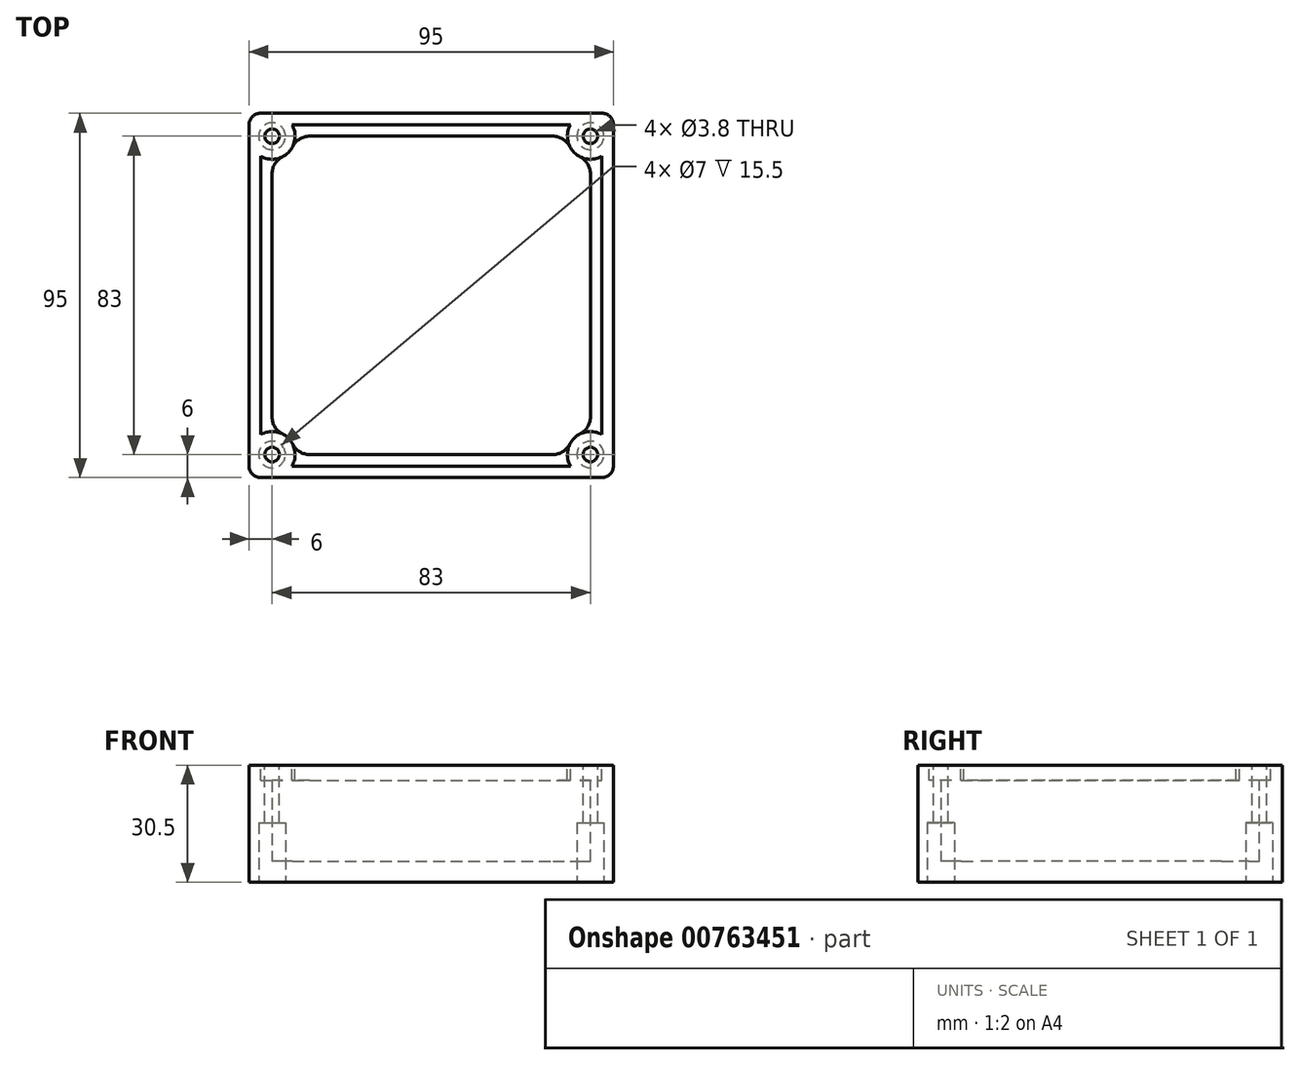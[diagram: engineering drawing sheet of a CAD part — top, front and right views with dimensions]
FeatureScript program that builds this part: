
annotation { "Feature Type Name" : "Feature", "Feature Type Description" : "" }
export const myFeature = defineFeature(function(context is Context, id is Id, definition is map)
    precondition{}
    {
        {
            var Q0;
            Q0=qCreatedBy(makeId("Top.planeOp"),FACE);
            var sketch = newSketch(context, id + "F0", { "sketchPlane" : qUnion([Q0])});
            skLineSegment(sketch, "E0.bottom", {"start": v(-47.5, 47.5) * mm, "end": v(47.5, 47.5) * mm});
            skLineSegment(sketch, "E0.top", {"start": v(-47.5, -47.5) * mm, "end": v(47.5, -47.5) * mm});
            skLineSegment(sketch, "E0.left", {"start": v(-47.5, 47.5) * mm, "end": v(-47.5, -47.5) * mm});
            skLineSegment(sketch, "E0.right", {"start": v(47.5, 47.5) * mm, "end": v(47.5, -47.5) * mm});
            skSolve(sketch);
        }
        {
            var Q0;
            Q0 = qSketchRegion(id + "F0", true);
            extrude(context, id + "F1", {"entities" : qUnion([Q0]), "depth" : 30.5 * mm, "offsetDistance" : 25 * mm});
        }
        {
            var Q0;
            Q0=makeQuery(id+"F1.opExtrude","CAP_FACE",FACE,{"disambiguationData":[OSD([sQuery(id+"F0.wireOp",EDGE,"E0.bottom"),sQuery(id+"F0.wireOp",EDGE,"E0.top"),sQuery(id+"F0.wireOp",EDGE,"E0.left"),sQuery(id+"F0.wireOp",EDGE,"E0.right")])],"isStart":false});
            var sketch = newSketch(context, id + "F2", { "sketchPlane" : qUnion([Q0])});
            skLineSegment(sketch, "E1.bottom", {"start": v(-47.5, 47.5) * mm, "end": v(-41.5, 47.5) * mm});
            skLineSegment(sketch, "E1.top", {"start": v(-47.5, 41.5) * mm, "end": v(-41.5, 41.5) * mm});
            skLineSegment(sketch, "E1.left", {"start": v(-47.5, 47.5) * mm, "end": v(-47.5, 41.5) * mm});
            skLineSegment(sketch, "E1.right", {"start": v(-41.5, 47.5) * mm, "end": v(-41.5, 41.5) * mm});
            skLineSegment(sketch, "E2.bottom", {"start": v(-47.5, -47.5) * mm, "end": v(-41.5, -47.5) * mm});
            skLineSegment(sketch, "E2.top", {"start": v(-47.5, -41.5) * mm, "end": v(-41.5, -41.5) * mm});
            skLineSegment(sketch, "E2.left", {"start": v(-47.5, -47.5) * mm, "end": v(-47.5, -41.5) * mm});
            skLineSegment(sketch, "E2.right", {"start": v(-41.5, -47.5) * mm, "end": v(-41.5, -41.5) * mm});
            skLineSegment(sketch, "E3.bottom", {"start": v(47.5, -47.5) * mm, "end": v(41.5, -47.5) * mm});
            skLineSegment(sketch, "E3.top", {"start": v(47.5, -41.5) * mm, "end": v(41.5, -41.5) * mm});
            skLineSegment(sketch, "E3.left", {"start": v(47.5, -47.5) * mm, "end": v(47.5, -41.5) * mm});
            skLineSegment(sketch, "E3.right", {"start": v(41.5, -47.5) * mm, "end": v(41.5, -41.5) * mm});
            skLineSegment(sketch, "E4.bottom", {"start": v(47.5, 47.5) * mm, "end": v(41.5, 47.5) * mm});
            skLineSegment(sketch, "E4.top", {"start": v(47.5, 41.5) * mm, "end": v(41.5, 41.5) * mm});
            skLineSegment(sketch, "E4.left", {"start": v(47.5, 47.5) * mm, "end": v(47.5, 41.5) * mm});
            skLineSegment(sketch, "E4.right", {"start": v(41.5, 47.5) * mm, "end": v(41.5, 41.5) * mm});
            skCircle(sketch, "E5", {"center": v(-41.5, 41.5) * mm, "radius": 6 * mm});
            skCircle(sketch, "E6", {"center": v(41.5, 41.5) * mm, "radius": 6 * mm});
            skCircle(sketch, "E7", {"center": v(41.5, -41.5) * mm, "radius": 6 * mm});
            skCircle(sketch, "E8", {"center": v(-41.5, -41.5) * mm, "radius": 6 * mm});
            skLineSegment(sketch, "E9.bottom", {"start": v(-47.5, 47.5) * mm, "end": v(-44.5, 47.5) * mm});
            skLineSegment(sketch, "E9.top", {"start": v(-47.5, -47.5) * mm, "end": v(-44.5, -47.5) * mm});
            skLineSegment(sketch, "E9.left", {"start": v(-47.5, 47.5) * mm, "end": v(-47.5, -47.5) * mm});
            skLineSegment(sketch, "E9.right", {"start": v(-44.5, 47.5) * mm, "end": v(-44.5, -47.5) * mm});
            skLineSegment(sketch, "E10.bottom", {"start": v(-47.5, -44.5) * mm, "end": v(47.5, -44.5) * mm});
            skLineSegment(sketch, "E10.top", {"start": v(-47.5, -47.5) * mm, "end": v(47.5, -47.5) * mm});
            skLineSegment(sketch, "E10.left", {"start": v(-47.5, -44.5) * mm, "end": v(-47.5, -47.5) * mm});
            skLineSegment(sketch, "E10.right", {"start": v(47.5, -44.5) * mm, "end": v(47.5, -47.5) * mm});
            skLineSegment(sketch, "E11.bottom", {"start": v(44.5, -47.5) * mm, "end": v(47.5, -47.5) * mm});
            skLineSegment(sketch, "E11.top", {"start": v(44.5, 47.5) * mm, "end": v(47.5, 47.5) * mm});
            skLineSegment(sketch, "E11.left", {"start": v(44.5, -47.5) * mm, "end": v(44.5, 47.5) * mm});
            skLineSegment(sketch, "E11.right", {"start": v(47.5, -47.5) * mm, "end": v(47.5, 47.5) * mm});
            skLineSegment(sketch, "E12.bottom", {"start": v(47.5, 44.5) * mm, "end": v(-47.5, 44.5) * mm});
            skLineSegment(sketch, "E12.top", {"start": v(47.5, 47.5) * mm, "end": v(-47.5, 47.5) * mm});
            skLineSegment(sketch, "E12.left", {"start": v(47.5, 44.5) * mm, "end": v(47.5, 47.5) * mm});
            skLineSegment(sketch, "E12.right", {"start": v(-47.5, 44.5) * mm, "end": v(-47.5, 47.5) * mm});
            skSolve(sketch);
        }
        {
            var Q0;
            {var subQ9=sQuery(id+"F2.wireOp",EDGE,"E12.bottom");var subQ10=sQuery(id+"F2.wireOp",EDGE,"E5");var subQ11=makeQuery(id+"F2.imprint","INTERSECT",VERTEX,{"disambiguationData":[OD(0.0)],"derivedFrom":[subQ10,subQ9]});Q0=makeQuery(id+"F2.imprint","IMPRINT",FACE,{"disambiguationData":[TD([[makeQuery(id+"F2.imprint","IMPRINT",EDGE,{"disambiguationData":[TD([[subQ11,1.0]])],"derivedFrom":subQ10}),-1.0]])]});}
            extrude(context, id + "F3", {"entities" : qUnion([Q0]), "operationType" : NewBodyOperationType.REMOVE, "oppositeDirection" : true, "depth" : 25 * mm, "offsetDistance" : 25 * mm});
        }
        {
            var Q0;
            Q0=makeQuery(id+"F1.opExtrude","CAP_FACE",FACE,{"disambiguationData":[OSD([sQuery(id+"F0.wireOp",EDGE,"E0.bottom"),sQuery(id+"F0.wireOp",EDGE,"E0.top"),sQuery(id+"F0.wireOp",EDGE,"E0.left"),sQuery(id+"F0.wireOp",EDGE,"E0.right")])],"isStart":false});
            var sketch = newSketch(context, id + "F4", { "sketchPlane" : qUnion([Q0])});
            skCircle(sketch, "E13", {"center": v(-41.5, 41.5) * mm, "radius": 1.9 * mm});
            skCircle(sketch, "E14", {"center": v(41.5, 41.5) * mm, "radius": 1.9 * mm});
            skCircle(sketch, "E15", {"center": v(-41.5, -41.5) * mm, "radius": 1.9 * mm});
            skCircle(sketch, "E16", {"center": v(41.5, -41.5) * mm, "radius": 1.9 * mm});
            skSolve(sketch);
        }
        {
            var Q0;
            Q0 = qSketchRegion(id + "F4", true);
            extrude(context, id + "F5", {"entities" : qUnion([Q0]), "operationType" : NewBodyOperationType.REMOVE, "endBound" : BoundingType.THROUGH_ALL, "oppositeDirection" : true, "depth" : 25 * mm, "offsetDistance" : 25 * mm});
        }
        {
            var Q0;
            Q0=makeQuery(id+"F1.opExtrude","SWEPT_EDGE",EDGE,{"disambiguationData":[OSD([sQuery(id+"F0.wireOp",EDGE,"E0.bottom"),sQuery(id+"F0.wireOp",EDGE,"E0.left")])]});
            var Q1;
            Q1=makeQuery(id+"F1.opExtrude","SWEPT_EDGE",EDGE,{"disambiguationData":[OSD([sQuery(id+"F0.wireOp",EDGE,"E0.bottom"),sQuery(id+"F0.wireOp",EDGE,"E0.right")])]});
            var Q2;
            Q2=makeQuery(id+"F1.opExtrude","SWEPT_EDGE",EDGE,{"disambiguationData":[OSD([sQuery(id+"F0.wireOp",EDGE,"E0.top"),sQuery(id+"F0.wireOp",EDGE,"E0.left")])]});
            var Q3;
            Q3=makeQuery(id+"F1.opExtrude","SWEPT_EDGE",EDGE,{"disambiguationData":[OSD([sQuery(id+"F0.wireOp",EDGE,"E0.top"),sQuery(id+"F0.wireOp",EDGE,"E0.right")])]});
            fillet(context, id + "F6", {"entities" : qUnion([Q0, Q1, Q2, Q3]), "radius" : 3 * mm, "tangentPropagation" : true, "allowEdgeOverflow" : false});
        }
        {
            var Q0;
            Q0=makeQuery(id+"F3.boolean.opBoolean","COPY",FACE,{"derivedFrom":makeQuery(id+"F3.opExtrude","CAP_FACE",FACE,{"disambiguationData":[OSD([sQuery(id+"F2.wireOp",EDGE,"E5"),sQuery(id+"F2.wireOp",EDGE,"E6"),sQuery(id+"F2.wireOp",EDGE,"E7"),sQuery(id+"F2.wireOp",EDGE,"E8"),sQuery(id+"F2.wireOp",EDGE,"E9.right"),sQuery(id+"F2.wireOp",EDGE,"E10.bottom"),sQuery(id+"F2.wireOp",EDGE,"E11.left"),sQuery(id+"F2.wireOp",EDGE,"E12.bottom")])],"isStart":false})});
            var sketch = newSketch(context, id + "F7", { "sketchPlane" : qUnion([Q0])});
            skLineSegment(sketch, "E17.bottom", {"start": v(-36.3, 44.5) * mm, "end": v(36.3, 44.5) * mm});
            skLineSegment(sketch, "E17.top", {"start": v(-36.3, 41.5) * mm, "end": v(36.3, 41.5) * mm});
            skLineSegment(sketch, "E17.left", {"start": v(-36.3, 44.5) * mm, "end": v(-36.3, 41.5) * mm});
            skLineSegment(sketch, "E17.right", {"start": v(36.3, 44.5) * mm, "end": v(36.3, 41.5) * mm});
            skLineSegment(sketch, "E18.bottom", {"start": v(-44.5, 36.3) * mm, "end": v(-41.5, 36.3) * mm});
            skLineSegment(sketch, "E18.top", {"start": v(-44.5, -36.3) * mm, "end": v(-41.5, -36.3) * mm});
            skLineSegment(sketch, "E18.left", {"start": v(-44.5, 36.3) * mm, "end": v(-44.5, -36.3) * mm});
            skLineSegment(sketch, "E18.right", {"start": v(-41.5, 36.3) * mm, "end": v(-41.5, -36.3) * mm});
            skLineSegment(sketch, "E19.bottom", {"start": v(-36.3, -44.5) * mm, "end": v(36.3, -44.5) * mm});
            skLineSegment(sketch, "E19.top", {"start": v(-36.3, -41.5) * mm, "end": v(36.3, -41.5) * mm});
            skLineSegment(sketch, "E19.left", {"start": v(-36.3, -44.5) * mm, "end": v(-36.3, -41.5) * mm});
            skLineSegment(sketch, "E19.right", {"start": v(36.3, -44.5) * mm, "end": v(36.3, -41.5) * mm});
            skLineSegment(sketch, "E20.bottom", {"start": v(44.5, 36.3) * mm, "end": v(41.5, 36.3) * mm});
            skLineSegment(sketch, "E20.top", {"start": v(44.5, -36.3) * mm, "end": v(41.5, -36.3) * mm});
            skLineSegment(sketch, "E20.left", {"start": v(44.5, 36.3) * mm, "end": v(44.5, -36.3) * mm});
            skLineSegment(sketch, "E20.right", {"start": v(41.5, 36.3) * mm, "end": v(41.5, -36.3) * mm});
            skSolve(sketch);
        }
        {
            var Q0;
            Q0 = qSketchRegion(id + "F7", true);
            extrude(context, id + "F8", {"entities" : qUnion([Q0]), "operationType" : NewBodyOperationType.ADD, "depth" : 21 * mm, "offsetDistance" : 25 * mm});
        }
        {
            var Q0;
            Q0=makeQuery(id+"F8.boolean.opBoolean","INTERSECT",EDGE,{"derivedFrom":[makeQuery(id+"F3.boolean.opBoolean","COPY",FACE,{"derivedFrom":makeQuery(id+"F3.opExtrude","SWEPT_FACE",FACE,{"disambiguationData":[OSD([sQuery(id+"F2.wireOp",EDGE,"E5")])]})}),makeQuery(id+"F8.opExtrude","SWEPT_FACE",FACE,{"disambiguationData":[OSD([sQuery(id+"F7.wireOp",EDGE,"E17.top")])]})]});
            var Q1;
            Q1=makeQuery(id+"F8.boolean.opBoolean","INTERSECT",EDGE,{"derivedFrom":[makeQuery(id+"F3.boolean.opBoolean","COPY",FACE,{"derivedFrom":makeQuery(id+"F3.opExtrude","SWEPT_FACE",FACE,{"disambiguationData":[OSD([sQuery(id+"F2.wireOp",EDGE,"E5")])]})}),makeQuery(id+"F8.opExtrude","SWEPT_FACE",FACE,{"disambiguationData":[OSD([sQuery(id+"F7.wireOp",EDGE,"E18.right")])]})]});
            var Q2;
            Q2=makeQuery(id+"F8.boolean.opBoolean","INTERSECT",EDGE,{"derivedFrom":[makeQuery(id+"F3.boolean.opBoolean","COPY",FACE,{"derivedFrom":makeQuery(id+"F3.opExtrude","SWEPT_FACE",FACE,{"disambiguationData":[OSD([sQuery(id+"F2.wireOp",EDGE,"E6")])]})}),makeQuery(id+"F8.opExtrude","SWEPT_FACE",FACE,{"disambiguationData":[OSD([sQuery(id+"F7.wireOp",EDGE,"E17.top")])]})]});
            var Q3;
            Q3=makeQuery(id+"F8.boolean.opBoolean","INTERSECT",EDGE,{"derivedFrom":[makeQuery(id+"F3.boolean.opBoolean","COPY",FACE,{"derivedFrom":makeQuery(id+"F3.opExtrude","SWEPT_FACE",FACE,{"disambiguationData":[OSD([sQuery(id+"F2.wireOp",EDGE,"E6")])]})}),makeQuery(id+"F8.opExtrude","SWEPT_FACE",FACE,{"disambiguationData":[OSD([sQuery(id+"F7.wireOp",EDGE,"E20.right")])]})]});
            var Q4;
            Q4=makeQuery(id+"F8.boolean.opBoolean","INTERSECT",EDGE,{"derivedFrom":[makeQuery(id+"F3.boolean.opBoolean","COPY",FACE,{"derivedFrom":makeQuery(id+"F3.opExtrude","SWEPT_FACE",FACE,{"disambiguationData":[OSD([sQuery(id+"F2.wireOp",EDGE,"E7")])]})}),makeQuery(id+"F8.opExtrude","SWEPT_FACE",FACE,{"disambiguationData":[OSD([sQuery(id+"F7.wireOp",EDGE,"E20.right")])]})]});
            var Q5;
            Q5=makeQuery(id+"F8.boolean.opBoolean","INTERSECT",EDGE,{"derivedFrom":[makeQuery(id+"F3.boolean.opBoolean","COPY",FACE,{"derivedFrom":makeQuery(id+"F3.opExtrude","SWEPT_FACE",FACE,{"disambiguationData":[OSD([sQuery(id+"F2.wireOp",EDGE,"E7")])]})}),makeQuery(id+"F8.opExtrude","SWEPT_FACE",FACE,{"disambiguationData":[OSD([sQuery(id+"F7.wireOp",EDGE,"E19.top")])]})]});
            var Q6;
            Q6=makeQuery(id+"F8.boolean.opBoolean","INTERSECT",EDGE,{"derivedFrom":[makeQuery(id+"F3.boolean.opBoolean","COPY",FACE,{"derivedFrom":makeQuery(id+"F3.opExtrude","SWEPT_FACE",FACE,{"disambiguationData":[OSD([sQuery(id+"F2.wireOp",EDGE,"E8")])]})}),makeQuery(id+"F8.opExtrude","SWEPT_FACE",FACE,{"disambiguationData":[OSD([sQuery(id+"F7.wireOp",EDGE,"E18.right")])]})]});
            var Q7;
            Q7=makeQuery(id+"F8.boolean.opBoolean","INTERSECT",EDGE,{"derivedFrom":[makeQuery(id+"F3.boolean.opBoolean","COPY",FACE,{"derivedFrom":makeQuery(id+"F3.opExtrude","SWEPT_FACE",FACE,{"disambiguationData":[OSD([sQuery(id+"F2.wireOp",EDGE,"E8")])]})}),makeQuery(id+"F8.opExtrude","SWEPT_FACE",FACE,{"disambiguationData":[OSD([sQuery(id+"F7.wireOp",EDGE,"E19.top")])]})]});
            fillet(context, id + "F9", {"entities" : qUnion([Q0, Q1, Q2, Q3, Q4, Q5, Q6, Q7]), "radius" : 5 * mm, "tangentPropagation" : true, "allowEdgeOverflow" : false});
        }
        {
            var Q0;
            Q0=makeQuery(id+"F1.opExtrude","CAP_FACE",FACE,{"disambiguationData":[OSD([sQuery(id+"F0.wireOp",EDGE,"E0.bottom"),sQuery(id+"F0.wireOp",EDGE,"E0.top"),sQuery(id+"F0.wireOp",EDGE,"E0.left"),sQuery(id+"F0.wireOp",EDGE,"E0.right")])],"isStart":true});
            var sketch = newSketch(context, id + "F10", { "sketchPlane" : qUnion([Q0])});
            skCircle(sketch, "E21", {"center": v(-41.5, 41.5) * mm, "radius": 3.5 * mm});
            skCircle(sketch, "E22", {"center": v(41.5, 41.5) * mm, "radius": 3.5 * mm});
            skCircle(sketch, "E23", {"center": v(-41.5, -41.5) * mm, "radius": 3.5 * mm});
            skCircle(sketch, "E24", {"center": v(41.5, -41.5) * mm, "radius": 3.5 * mm});
            skSolve(sketch);
        }
        {
            var Q0;
            Q0 = qSketchRegion(id + "F10", true);
            extrude(context, id + "F11", {"entities" : qUnion([Q0]), "operationType" : NewBodyOperationType.REMOVE, "oppositeDirection" : true, "depth" : 15.5 * mm, "offsetDistance" : 25 * mm});
        }
    });
